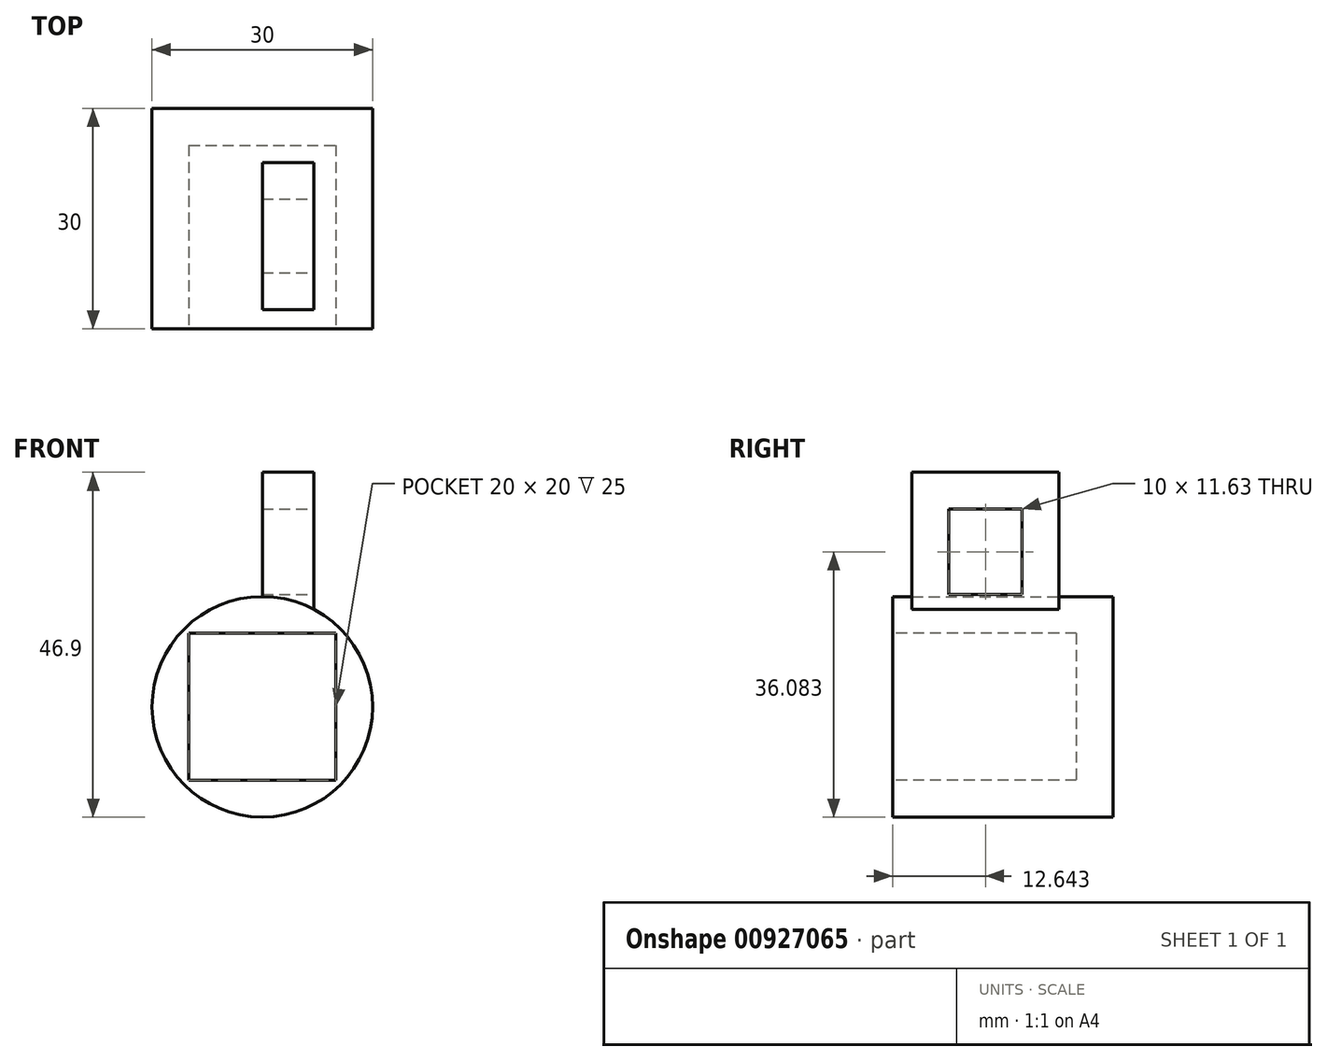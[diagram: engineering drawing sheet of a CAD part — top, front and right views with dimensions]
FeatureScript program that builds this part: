
annotation { "Feature Type Name" : "Feature", "Feature Type Description" : "" }
export const myFeature = defineFeature(function(context is Context, id is Id, definition is map)
    precondition{}
    {
        {
            var Q0;
            Q0=qCreatedBy(makeId("Front.planeOp"),FACE);
            var sketch = newSketch(context, id + "F0", { "sketchPlane" : qUnion([Q0])});
            skCircle(sketch, "E0", {"center": v(0, 0) * mm, "radius": 15 * mm});
            skSolve(sketch);
        }
        {
            var Q0;
            Q0=makeQuery(id+"F0.imprint","IMPRINT",FACE,{"disambiguationData":[TD([[makeQuery(id+"F0.imprint","IMPRINT",EDGE,{"derivedFrom":sQuery(id+"F0.wireOp",EDGE,"E0")}),1.0]])]});
            extrude(context, id + "F1", {"entities" : qUnion([Q0]), "depth" : 30 * mm, "offsetDistance" : 25 * mm});
        }
        {
            var Q0;
            Q0=makeQuery(id+"F1.opExtrude","CAP_FACE",FACE,{"disambiguationData":[OSD([sQuery(id+"F0.wireOp",EDGE,"E0")])],"isStart":false});
            var sketch = newSketch(context, id + "F2", { "sketchPlane" : qUnion([Q0])});
            skLineSegment(sketch, "E1.bottom", {"start": v(-10, 10) * mm, "end": v(10, 10) * mm});
            skLineSegment(sketch, "E1.top", {"start": v(-10, -10) * mm, "end": v(10, -10) * mm});
            skLineSegment(sketch, "E1.left", {"start": v(-10, 10) * mm, "end": v(-10, -10) * mm});
            skLineSegment(sketch, "E1.right", {"start": v(10, 10) * mm, "end": v(10, -10) * mm});
            skPoint(sketch, "E1.middle", {"position": v(0, 0) * mm});
            skSolve(sketch);
        }
        {
            var Q0;
            Q0=makeQuery(id+"F2.imprint","IMPRINT",FACE,{"disambiguationData":[TD([[makeQuery(id+"F2.imprint","IMPRINT",EDGE,{"derivedFrom":sQuery(id+"F2.wireOp",EDGE,"E1.bottom")}),-1.0]])]});
            extrude(context, id + "F3", {"entities" : qUnion([Q0]), "operationType" : NewBodyOperationType.REMOVE, "oppositeDirection" : true, "depth" : 25 * mm, "offsetDistance" : 25 * mm});
        }
        {
            var Q0;
            Q0=qCreatedBy(makeId("Right.planeOp"),FACE);
            var sketch = newSketch(context, id + "F4", { "sketchPlane" : qUnion([Q0])});
            skLineSegment(sketch, "E2.bottom", {"start": v(-27.36, 11.9) * mm, "end": v(-7.36, 11.9) * mm});
            skLineSegment(sketch, "E2.top", {"start": v(-27.36, 31.9) * mm, "end": v(-7.36, 31.9) * mm});
            skLineSegment(sketch, "E2.left", {"start": v(-27.36, 11.9) * mm, "end": v(-27.36, 31.9) * mm});
            skLineSegment(sketch, "E2.right", {"start": v(-7.36, 11.9) * mm, "end": v(-7.36, 31.9) * mm});
            skSolve(sketch);
        }
        {
            var Q0;
            Q0=makeQuery(id+"F4.imprint","IMPRINT",FACE,{"disambiguationData":[TD([[makeQuery(id+"F4.imprint","IMPRINT",EDGE,{"derivedFrom":sQuery(id+"F4.wireOp",EDGE,"E2.bottom")}),1.0]])]});
            extrude(context, id + "F5", {"entities" : qUnion([Q0]), "operationType" : NewBodyOperationType.ADD, "depth" : 7 * mm, "offsetDistance" : 25 * mm});
        }
        {
            var Q0;
            Q0=makeQuery(id+"F5.opExtrude","CAP_FACE",FACE,{"disambiguationData":[OSD([sQuery(id+"F4.wireOp",EDGE,"E2.bottom"),sQuery(id+"F4.wireOp",EDGE,"E2.top"),sQuery(id+"F4.wireOp",EDGE,"E2.left"),sQuery(id+"F4.wireOp",EDGE,"E2.right")])],"isStart":false});
            var sketch = newSketch(context, id + "F6", { "sketchPlane" : qUnion([Q0])});
            skLineSegment(sketch, "E3.bottom", {"start": v(-22.36, 15.27) * mm, "end": v(-12.36, 15.27) * mm});
            skLineSegment(sketch, "E3.top", {"start": v(-22.36, 26.9) * mm, "end": v(-12.36, 26.9) * mm});
            skLineSegment(sketch, "E3.left", {"start": v(-22.36, 15.27) * mm, "end": v(-22.36, 26.9) * mm});
            skLineSegment(sketch, "E3.right", {"start": v(-12.36, 15.27) * mm, "end": v(-12.36, 26.9) * mm});
            skSolve(sketch);
        }
        {
            var Q0;
            Q0=makeQuery(id+"F6.imprint","IMPRINT",FACE,{"disambiguationData":[TD([[makeQuery(id+"F6.imprint","IMPRINT",EDGE,{"derivedFrom":sQuery(id+"F6.wireOp",EDGE,"E3.bottom")}),1.0]])]});
            extrude(context, id + "F7", {"entities" : qUnion([Q0]), "operationType" : NewBodyOperationType.REMOVE, "oppositeDirection" : true, "depth" : 20 * mm, "offsetDistance" : 25 * mm});
        }
    });
